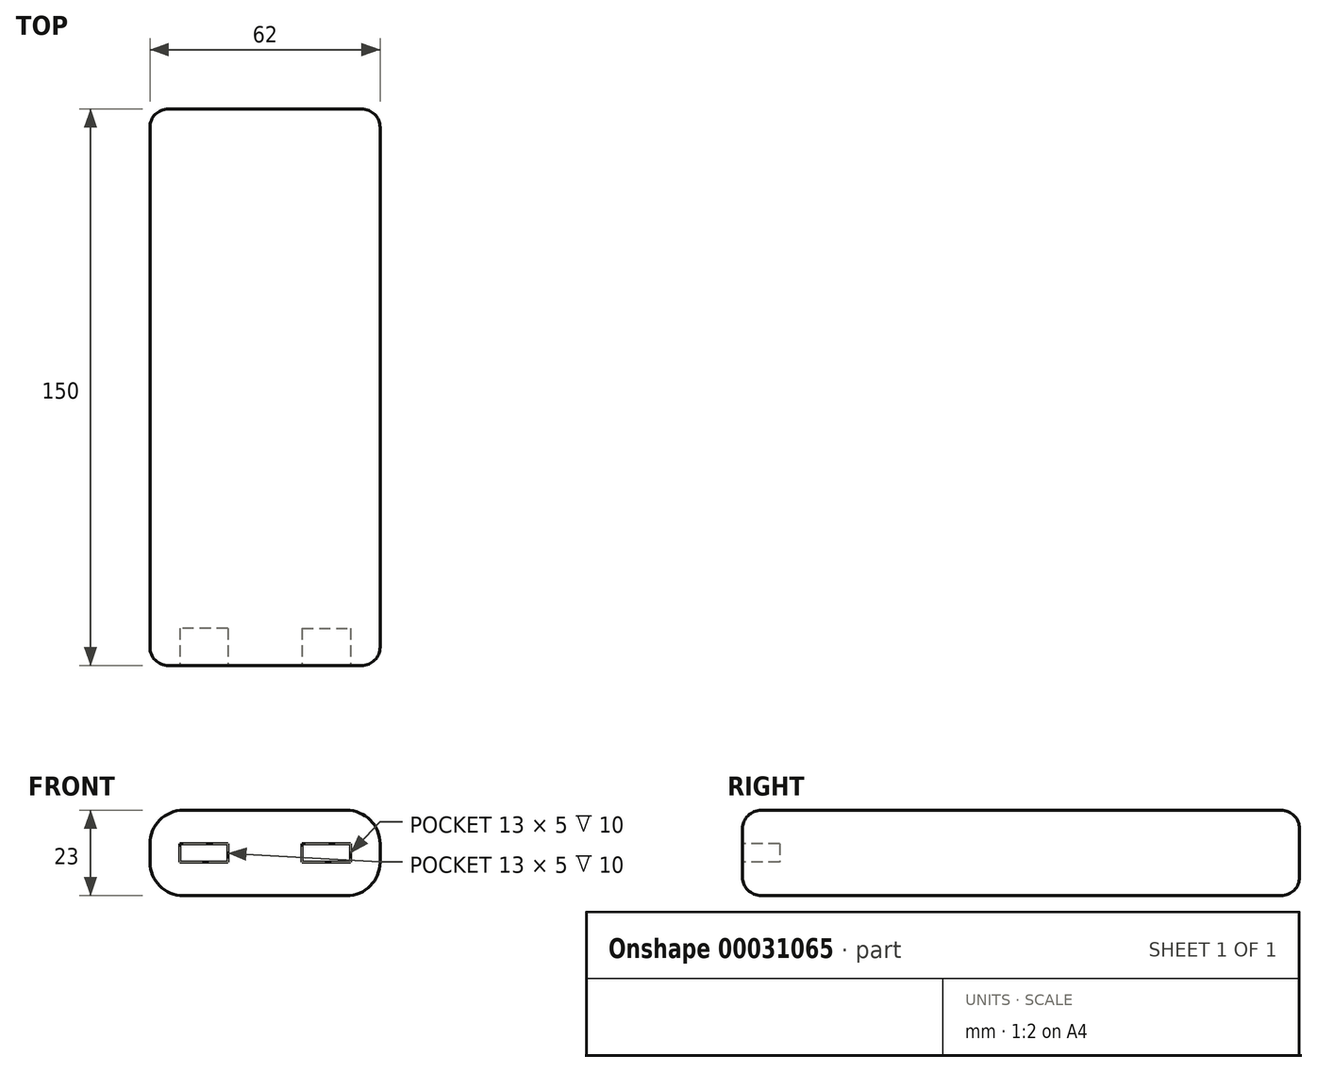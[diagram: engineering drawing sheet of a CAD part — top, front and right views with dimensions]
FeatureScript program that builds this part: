
annotation { "Feature Type Name" : "Feature", "Feature Type Description" : "" }
export const myFeature = defineFeature(function(context is Context, id is Id, definition is map)
    precondition{}
    {
        {
            var Q0;
            Q0=qCreatedBy(makeId("Front.planeOp"),FACE);
            var sketch = newSketch(context, id + "F0", { "sketchPlane" : qUnion([Q0])});
            skLineSegment(sketch, "E0.rect.bottom", {"start": v(31, -11.5) * mm, "end": v(-31, -11.5) * mm});
            skLineSegment(sketch, "E0.rect.top", {"start": v(31, 11.5) * mm, "end": v(-31, 11.5) * mm});
            skLineSegment(sketch, "E0.rect.left", {"start": v(31, -11.5) * mm, "end": v(31, 11.5) * mm});
            skLineSegment(sketch, "E0.rect.right", {"start": v(-31, -11.5) * mm, "end": v(-31, 11.5) * mm});
            skPoint(sketch, "E0.rect.middle", {"position": v(0, 0) * mm});
            skSolve(sketch);
        }
        {
            var Q0;
            Q0=makeQuery(id+"F0.imprint","IMPRINT",FACE,{"disambiguationData":[TD([[makeQuery(id+"F0.imprint","IMPRINT",EDGE,{"derivedFrom":sQuery(id+"F0.wireOp",EDGE,"E0.rect.bottom")}),-1.0]])]});
            extrude(context, id + "F1", {"entities" : qUnion([Q0]), "depth" : 150 / 2 * mm, "hasSecondDirection" : true, "secondDirectionOppositeDirection" : true, "secondDirectionDepth" : (150 / 2) * mm});
        }
        {
            var Q0;
            Q0=makeQuery(id+"F1.opExtrude","SWEPT_EDGE",EDGE,{"disambiguationData":[OSD([sQuery(id+"F0.wireOp",EDGE,"E0.rect.top"),sQuery(id+"F0.wireOp",EDGE,"E0.rect.left")])]});
            var Q1;
            Q1=makeQuery(id+"F1.opExtrude","SWEPT_EDGE",EDGE,{"disambiguationData":[OSD([sQuery(id+"F0.wireOp",EDGE,"E0.rect.bottom"),sQuery(id+"F0.wireOp",EDGE,"E0.rect.left")])]});
            var Q2;
            Q2=makeQuery(id+"F1.opExtrude","SWEPT_EDGE",EDGE,{"disambiguationData":[OSD([sQuery(id+"F0.wireOp",EDGE,"E0.rect.top"),sQuery(id+"F0.wireOp",EDGE,"E0.rect.right")])]});
            var Q3;
            Q3=makeQuery(id+"F1.opExtrude","SWEPT_EDGE",EDGE,{"disambiguationData":[OSD([sQuery(id+"F0.wireOp",EDGE,"E0.rect.bottom"),sQuery(id+"F0.wireOp",EDGE,"E0.rect.right")])]});
            fillet(context, id + "F2", {"entities" : qUnion([Q0, Q1, Q2, Q3]), "radius" : 9 * mm, "tangentPropagation" : true, "allowEdgeOverflow" : false});
        }
        {
            var Q0;
            Q0=makeQuery(id+"F1.opExtrude","CAP_FACE",FACE,{"disambiguationData":[OSD([sQuery(id+"F0.wireOp",EDGE,"E0.rect.bottom"),sQuery(id+"F0.wireOp",EDGE,"E0.rect.top"),sQuery(id+"F0.wireOp",EDGE,"E0.rect.left"),sQuery(id+"F0.wireOp",EDGE,"E0.rect.right")])],"isStart":false});
            var Q1;
            Q1=makeQuery(id+"F1.opExtrude","CAP_FACE",FACE,{"disambiguationData":[OSD([sQuery(id+"F0.wireOp",EDGE,"E0.rect.bottom"),sQuery(id+"F0.wireOp",EDGE,"E0.rect.top"),sQuery(id+"F0.wireOp",EDGE,"E0.rect.left"),sQuery(id+"F0.wireOp",EDGE,"E0.rect.right")])],"isStart":true});
            fillet(context, id + "F3", {"entities" : qUnion([Q0, Q1]), "radius" : 5 * mm, "tangentPropagation" : true, "allowEdgeOverflow" : false});
        }
        {
            var Q0;
            Q0=makeQuery(id+"F1.opExtrude","CAP_FACE",FACE,{"disambiguationData":[OSD([sQuery(id+"F0.wireOp",EDGE,"E0.rect.bottom"),sQuery(id+"F0.wireOp",EDGE,"E0.rect.top"),sQuery(id+"F0.wireOp",EDGE,"E0.rect.left"),sQuery(id+"F0.wireOp",EDGE,"E0.rect.right")])],"isStart":false});
            var sketch = newSketch(context, id + "F4", { "sketchPlane" : qUnion([Q0])});
            skLineSegment(sketch, "E1.bottom", {"start": v(10, 2.5) * mm, "end": v(23, 2.5) * mm});
            skLineSegment(sketch, "E1.top", {"start": v(10, -2.5) * mm, "end": v(23, -2.5) * mm});
            skLineSegment(sketch, "E1.left", {"start": v(10, 2.5) * mm, "end": v(10, -2.5) * mm});
            skLineSegment(sketch, "E1.right", {"start": v(23, 2.5) * mm, "end": v(23, -2.5) * mm});
            skLineSegment(sketch, "E2.MirrorCS", {"start": v(-10, 2.5) * mm, "end": v(-23, 2.5) * mm});
            skLineSegment(sketch, "E3.MirrorCS", {"start": v(-10, -2.5) * mm, "end": v(-23, -2.5) * mm});
            skLineSegment(sketch, "E4.MirrorCS", {"start": v(-23, 2.5) * mm, "end": v(-23, -2.5) * mm});
            skLineSegment(sketch, "E5.MirrorCS", {"start": v(-10, 2.5) * mm, "end": v(-10, -2.5) * mm});
            skSolve(sketch);
        }
        {
            var Q0;
            Q0=makeQuery(id+"F4.imprint","IMPRINT",FACE,{"disambiguationData":[TD([[makeQuery(id+"F4.imprint","IMPRINT",EDGE,{"derivedFrom":sQuery(id+"F4.wireOp",EDGE,"E2.MirrorCS")}),1.0]])]});
            var Q1;
            Q1=makeQuery(id+"F4.imprint","IMPRINT",FACE,{"disambiguationData":[TD([[makeQuery(id+"F4.imprint","IMPRINT",EDGE,{"derivedFrom":sQuery(id+"F4.wireOp",EDGE,"E1.bottom")}),-1.0]])]});
            extrude(context, id + "F5", {"entities" : qUnion([Q0, Q1]), "operationType" : NewBodyOperationType.REMOVE, "oppositeDirection" : true, "depth" : 10 * mm});
        }
    });
